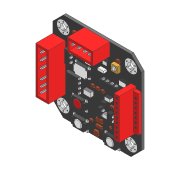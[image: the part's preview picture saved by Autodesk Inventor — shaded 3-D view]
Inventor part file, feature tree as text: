
AUTODESK INVENTOR PART (.ipt)
format: ipt  version: 2022 (Build 260153000, 153)  size: 1,719,808 bytes
history: native  units: mm
features: projected_geometry x48, extrude x15, sketch x15, fillet x1
ambient origin geometry x8: Origin, YZ Plane, XZ Plane, XY Plane, X Axis, Y Axis, Z Axis, Center Point
bodies: Solid1 (feature_tree)
feature tree (79):
  extrude  "Extrusion1"  Depth=1.25mm TaperAngle=0.0deg
  extrude  "Extrusion2"  Depth=60.0mm TaperAngle=360.0deg
  extrude  "Extrusion3"  Depth=60.0mm TaperAngle=360.0deg
  extrude  "Extrusion4"  Depth=1.5mm TaperAngle=0.0deg
  extrude  "Extrusion5"  Depth=1.75mm TaperAngle=0.0deg
  extrude  "Extrusion6"  Depth=1.75mm TaperAngle=0.0deg
  extrude  "Extrusion7"  Depth=1.0mm TaperAngle=0.0deg
  extrude  "Extrusion8"  Depth=5.5mm TaperAngle=0.0deg
  extrude  "Extrusion9"  Depth=0.005mm TaperAngle=0.0deg
  fillet  "Fillet1"  Radius=0.005mm
  extrude  "Extrusion10"  Depth=0.75mm TaperAngle=0.0deg
  extrude  "Extrusion11"  [1 undecoded]
  extrude  "Extrusion12"  [1 undecoded]
  extrude  "Extrusion13"  [1 undecoded]
  extrude  "Extrusion14"  [1 undecoded]
  extrude  "Extrusion15"  [1 undecoded]
  sketch  "Sketch1"  dims[d0=40.0mm d2=360.0deg d4=1.25mm d5=0.0mm]
  sketch  "Sketch2"  dims[d6=60.0mm d8=360.0deg d11=60.0mm d12=360.0deg]
  sketch  "Sketch3"  dims[d14=60.0mm d16=60.0mm d17=360.0deg d19=60.0mm d21=60.0mm d23=60.0mm d24=360.0deg]
  sketch  "Sketch4"  dims[d25=0.05mm d26=0.0mm d27=1.5mm d28=0.0mm]
  projected_geometry  "Projected Loop1"
  projected_geometry  "Projected Loop2"
  projected_geometry  "Projected Loop3"
  projected_geometry  "Projected Loop4"
  projected_geometry  "Projected Loop5"
  projected_geometry  "Projected Loop6"
  projected_geometry  "Projected Loop7"
  projected_geometry  "Projected Loop8"
  projected_geometry  "Projected Loop9"
  projected_geometry  "Projected Loop10"
  projected_geometry  "Projected Loop11"
  projected_geometry  "Projected Loop12"
  projected_geometry  "Projected Loop13"
  projected_geometry  "Projected Loop14"
  projected_geometry  "Projected Loop15"
  projected_geometry  "Projected Loop16"
  sketch  "Sketch5"  dims[d29=1.0mm d30=0.0mm d31=1.75mm d32=0.0mm]
  projected_geometry  "Projected Loop17"
  projected_geometry  "Projected Loop18"
  projected_geometry  "Projected Loop19"
  projected_geometry  "Projected Loop20"
  projected_geometry  "Projected Loop21"
  projected_geometry  "Projected Loop22"
  sketch  "Sketch6"  dims[d33=1.75mm d34=0.0mm d35=1.75mm d36=0.0mm]
  projected_geometry  "Projected Loop23"
  projected_geometry  "Projected Loop24"
  projected_geometry  "Projected Loop25"
  projected_geometry  "Projected Loop26"
  projected_geometry  "Projected Loop27"
  sketch  "Sketch7"  dims[d37=1.0mm d38=0.0mm d39=1.0mm d40=0.0mm]
  projected_geometry  "Projected Loop28"
  projected_geometry  "Projected Loop29"
  projected_geometry  "Projected Loop30"
  projected_geometry  "Projected Loop31"
  sketch  "Sketch8"  dims[d41=0.25mm d42=5.5mm d43=0.0mm]
  projected_geometry  "Projected Loop32"
  projected_geometry  "Projected Loop33"
  projected_geometry  "Projected Loop34"
  projected_geometry  "Projected Loop35"
  projected_geometry  "Projected Loop36"
  projected_geometry  "Projected Loop37"
  projected_geometry  "Projected Loop38"
  sketch  "Sketch9"  dims[d44=0.005mm d45=0.0mm d46=0.005mm d47=0.0mm d48=0.005mm d49=0.0mm]
  projected_geometry  "Projected Loop39"
  projected_geometry  "Projected Loop40"
  projected_geometry  "Projected Loop41"
  projected_geometry  "Projected Loop42"
  sketch  "Sketch10"  dims[d50=1.0mm d51=0.0mm d52=0.75mm d53=0.0mm]
  projected_geometry  "Projected Loop43"
  projected_geometry  "Projected Loop44"
  projected_geometry  "Projected Loop45"
  projected_geometry  "Projected Loop46"
  sketch  "Sketch11"
  sketch  "Sketch12"
  sketch  "Sketch13"
  sketch  "Sketch14"
  projected_geometry  "Projected Loop47"
  projected_geometry  "Projected Loop48"
  sketch  "Sketch15"
note: 5 required parameter values undecoded (feature->parameter linkage not recoverable at this tier; creation-order binding heuristic only, values carry confidence <= 0.55)
